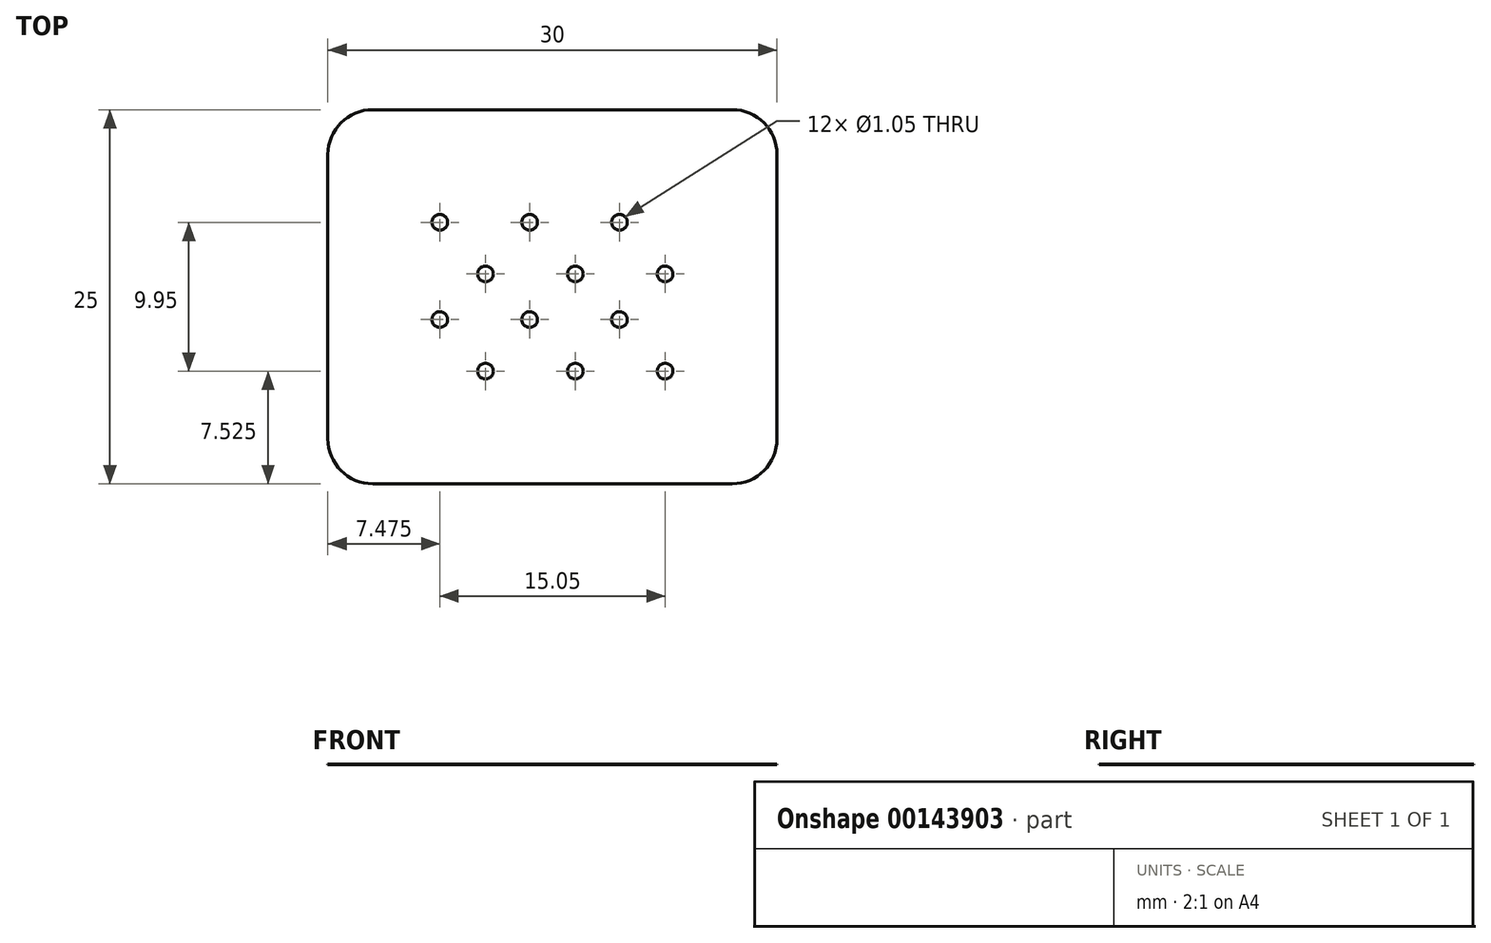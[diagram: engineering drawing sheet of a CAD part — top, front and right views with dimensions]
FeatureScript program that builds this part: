
annotation { "Feature Type Name" : "Feature", "Feature Type Description" : "" }
export const myFeature = defineFeature(function(context is Context, id is Id, definition is map)
    precondition{}
    {
        {
            var Q0;
            Q0=qCreatedBy(makeId("Top.planeOp"),FACE);
            var sketch = newSketch(context, id + "F0", { "sketchPlane" : qUnion([Q0])});
            skCircle(sketch, "E0", {"center": v(-1.52, 4.97) * mm, "radius": 0.53 * mm});
            skCircle(sketch, "E1", {"center": v(1.52, 1.52) * mm, "radius": 0.53 * mm});
            skCircle(sketch, "E2", {"center": v(-1.52, -1.52) * mm, "radius": 0.53 * mm});
            skCircle(sketch, "E3", {"center": v(1.52, -4.97) * mm, "radius": 0.53 * mm});
            skCircle(sketch, "E4.1.0.0", {"center": v(7.53, -4.97) * mm, "radius": 0.53 * mm});
            skCircle(sketch, "E4.1.0.1", {"center": v(4.47, -1.52) * mm, "radius": 0.53 * mm});
            skCircle(sketch, "E4.1.0.2", {"center": v(7.53, 1.52) * mm, "radius": 0.53 * mm});
            skCircle(sketch, "E4.1.0.3", {"center": v(4.47, 4.97) * mm, "radius": 0.53 * mm});
            skCircle(sketch, "E4.2.0.0", {"center": v(13.53, -4.97) * mm, "radius": 0.53 * mm});
            skCircle(sketch, "E4.2.0.1", {"center": v(10.47, -1.52) * mm, "radius": 0.53 * mm});
            skCircle(sketch, "E4.2.0.2", {"center": v(13.53, 1.52) * mm, "radius": 0.53 * mm});
            skCircle(sketch, "E4.2.0.3", {"center": v(10.47, 4.97) * mm, "radius": 0.53 * mm});
            skLineSegment(sketch, "E4.direction1", {"start": v(1.52, -4.97) * mm, "end": v(7.53, -4.97) * mm, "construction": true});
            skLineSegment(sketch, "E5.bottom", {"start": v(18, -12.5) * mm, "end": v(-6, -12.5) * mm});
            skLineSegment(sketch, "E5.top", {"start": v(18, 12.5) * mm, "end": v(-6, 12.5) * mm});
            skLineSegment(sketch, "E5.left", {"start": v(21, -9.5) * mm, "end": v(21, 9.5) * mm});
            skLineSegment(sketch, "E5.right", {"start": v(-9, -9.5) * mm, "end": v(-9, 9.5) * mm});
            skPoint(sketch, "E5.middle", {"position": v(6, 0) * mm});
            skPoint(sketch, "E6.visualSharp", {"position": v(-9, 12.5) * mm});
            skArc(sketch, "E6.filletArc", {"start": v(-6, 12.5) * mm, "mid": v(-8.12, 11.62) * mm, "end": v(-9, 9.5) * mm});
            skPoint(sketch, "E7.visualSharp", {"position": v(21, 12.5) * mm});
            skArc(sketch, "E7.filletArc", {"start": v(21, 9.5) * mm, "mid": v(20.12, 11.62) * mm, "end": v(18, 12.5) * mm});
            skPoint(sketch, "E8.visualSharp", {"position": v(21, -12.5) * mm});
            skArc(sketch, "E8.filletArc", {"start": v(18, -12.5) * mm, "mid": v(20.12, -11.62) * mm, "end": v(21, -9.5) * mm});
            skPoint(sketch, "E9.visualSharp", {"position": v(-9, -12.5) * mm});
            skArc(sketch, "E9.filletArc", {"start": v(-9, -9.5) * mm, "mid": v(-8.12, -11.62) * mm, "end": v(-6, -12.5) * mm});
            skSolve(sketch);
        }
        {
            var Q0;
            Q0=makeQuery(id+"F0.imprint","IMPRINT",FACE,{"disambiguationData":[TD([[makeQuery(id+"F0.imprint","IMPRINT",EDGE,{"derivedFrom":sQuery(id+"F0.wireOp",EDGE,"E0")}),-1.0]])]});
            extrude(context, id + "F1", {"entities" : qUnion([Q0]), "depth" : 1 / 203.2 * mm});
        }
    });
